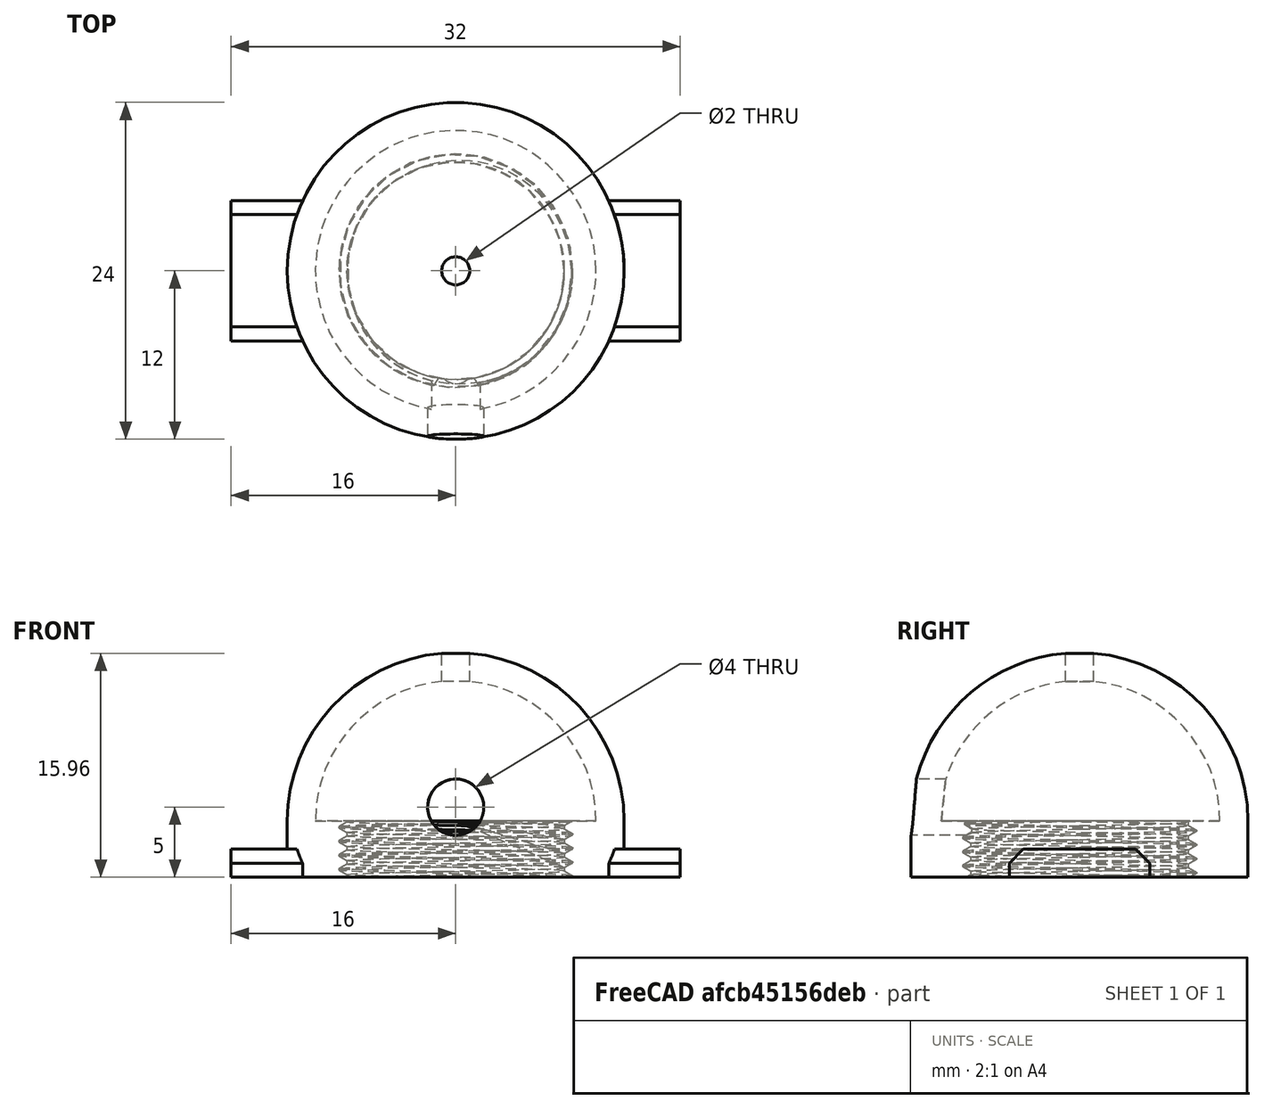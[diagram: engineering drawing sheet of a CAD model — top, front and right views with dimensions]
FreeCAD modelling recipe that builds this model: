
FCSTD DOCUMENT  (FreeCAD 0.18.4R)
Label: oxymetre-reducteur_de_flux
License: All rights reserved
LicenseURL: http://en.wikipedia.org/wiki/All_rights_reserved
objects: Part::Cylinder×3, Part::Sphere×2, Part::Box×2, Part::MultiFuse×2, Part::FeaturePython×1, Part::Cut×1, Part::Chamfer×1, Mesh::Feature×1
note: 12 computed .brp shape members not serialized (recipe doc carries the construction recipe); baked Part::Feature solids carry a one-line shape summary decoded from their .brp

FEATURE [Part::Sphere] Sphere
  Angle1 = 0
  Angle2 = 90
  Angle3 = 360
  AttacherType = Attacher::AttachEngine3D
  Radius = 12
FEATURE [Part::Sphere] Sphere001
  Angle1 = 0
  Angle2 = 90
  Angle3 = 360
  AttacherType = Attacher::AttachEngine3D
  Radius = 10
FEATURE [Part::Cylinder] Cylinder
  Angle = 360
  AttacherType = Attacher::AttachEngine3D
  Height = 10
  Placement = pos=(0,0,6) rot=(0,0,1;0rad)
  Radius = 1
FEATURE [Part::Cylinder] Cylinder001
  Angle = 360
  AttacherType = Attacher::AttachEngine3D
  Height = 17
  Placement = pos=(0,0,1) rot=(1,0,0;1.5708rad)
  Radius = 2
FEATURE [Part::Cylinder] Cylinder002
  Angle = 360
  AttacherType = Attacher::AttachEngine3D
  Height = 4
  Placement = pos=(0,0,-4) rot=(0,0,1;0rad)
  Radius = 12
FEATURE [Part::Box] Box  label="Cube"
  AttacherType = Attacher::AttachEngine3D
  Height = 2
  Length = 6
  Placement = pos=(10,-5,-4) rot=(0,0,1;0rad)
  Width = 10
FEATURE [Part::Box] Box001  label="Cube001"
  AttacherType = Attacher::AttachEngine3D
  Height = 2
  Length = 6
  Placement = pos=(-16,-5,-4) rot=(0,0,1;0rad)
  Width = 10
FEATURE [Part::MultiFuse] Fusion  label="externe"
  Refine = true
  Shapes = -> [Sphere,Cylinder002,Box,Box001]
FEATURE [Part::FeaturePython] ScrewTap  label="M16x4.0-ScrewTap"  # Fasteners workbench fastener (typed FeaturePython)
  diameter = 13
  invert = false
  length = 4
  matchOuter = false
  offset = 0
  thread = true
FEATURE [Part::MultiFuse] Fusion001  label="interne et trous"
  Refine = true
  Shapes = -> [Cylinder001,Sphere001,Cylinder,ScrewTap]
FEATURE [Part::Cut] Cut  label="complet"
  Base = -> Fusion
  Refine = true
  Tool = -> Fusion001
FEATURE [Part::Chamfer] Chamfer
  Base = -> Cut
  Edges = 4 edges r=1: [Edge37,Edge39,Edge51,Edge53]
FEATURE [Mesh::Feature] Mesh  label="Chamfer (Meshed)"
